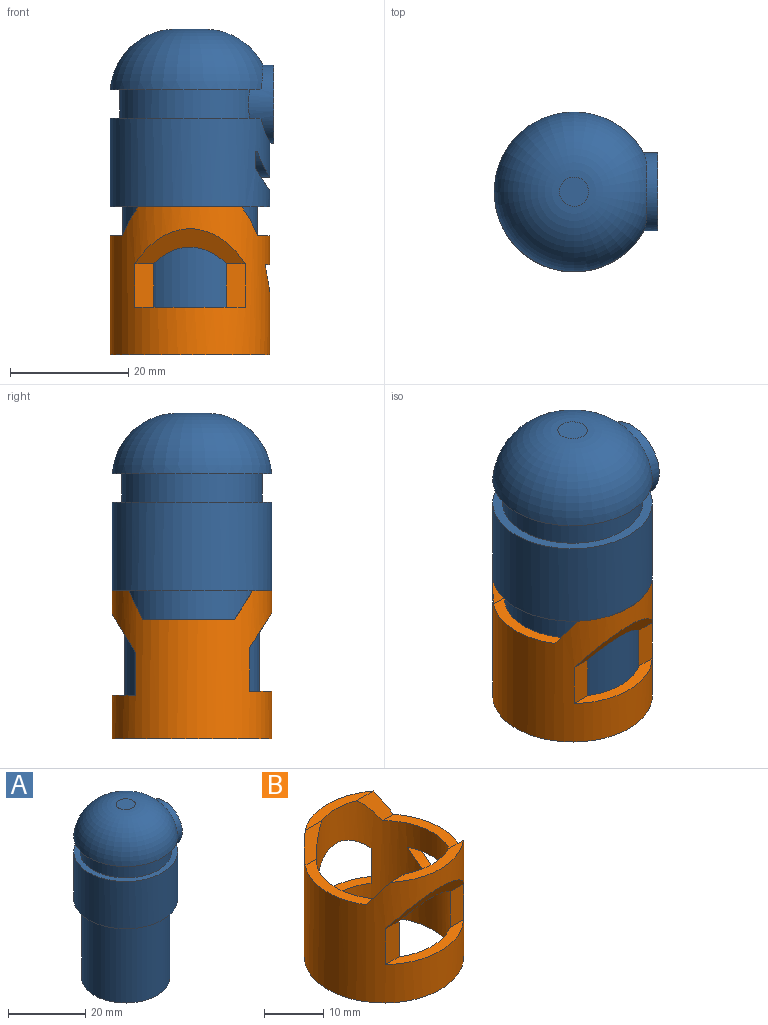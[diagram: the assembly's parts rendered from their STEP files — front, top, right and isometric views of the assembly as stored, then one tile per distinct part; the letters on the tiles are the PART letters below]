
ASSEMBLY  parts=2 mates=1
PART A: 18 faces, bbox 27.6x27x55 mm
  f0: torus R=2.48mm, axis (0,0,-1), area 927.2mm2, adj f1,f6,f7
  f1: plane 4.95x4.95mm, normal (0,0,1), area 19.3mm2, adj f0
  f2: plane 26.95x26.95mm, normal (0,0,-1), area 162.2mm2, adj f3,f16
  f3: cylinder r=13.48mm len=26.95mm, axis (0,0,-1), area 1189.7mm2, adj f2,f4,f7,f11,f12,f13,f14,f15
  f4: plane 26.95x25.47mm, normal (0,0,1), area 108.7mm2, adj f3,f5,f7
  f5: cylinder r=11.85mm len=23.69mm, axis (0,0,-1), area 289.4mm2, adj f4,f6,f7
  f6: plane 26.95x25.47mm, normal (0,0,-1), area 108.7mm2, adj f0,f5,f7
  f7: cylinder r=6.59mm len=13.18mm, axis (-1,0,0), area 91.5mm2, adj f0,f3,f4,f5,f6,f8
  f8: plane 13.18x13.18mm, normal (1,0,0), area 53.8mm2, adj f7,f9
  f9: cylinder r=5.13mm len=10.26mm, axis (1,0,0), area 93.4mm2, adj f8,f10
  f10: plane 10.26x10.26mm, normal (1,0,0), area 82.6mm2, adj f9
  f11: plane 0.53x0.35mm, normal (0,0,-1), area 0.1mm2, adj f3,f14,f15
  f12: cylinder r=9.85mm len=15.44mm, axis (1,0,0), area 27.6mm2, adj f3,f15
  f13: plane 0.53x0.35mm, normal (0,0,-1), area 0.1mm2, adj f3,f14,f15
  f14: cylinder r=8.06mm len=14.38mm, axis (1,0,0), area 28.9mm2, adj f3,f11,f13,f15
  f15: plane 15.44x6.59mm, normal (1,0,0), area 38.8mm2, adj f3,f11,f12,f13,f14
  f16: cylinder r=11.4mm len=25mm, axis (0,0,1), area 1790.7mm2, adj f2,f17
  f17: plane 22.8x22.8mm, normal (0,0,-1), area 408.3mm2, adj f16
PART B: 23 faces, bbox 27x27x25 mm
  f0: cylinder r=13.48mm len=26.96mm, axis (0,0,1), area 1415.5mm2, adj f2,f3,f4,f5,f6,f7,f8,f9
  f1: cylinder r=11.5mm len=25mm, axis (0,0,1), area 1322mm2, adj f2,f3,f4,f5,f6,f7,f8,f9
  f2: plane 7.42x3.21mm, normal (0,-1,0), area 23.8mm2, adj f0,f1,f10,f11
  f3: plane 7.29x3.1mm, normal (0,1,0), area 22.6mm2, adj f0,f1,f13,f15
  f4: plane 6.47x4.85mm, normal (0,-0.9,0.44), area 17.2mm2, adj f0,f1,f6,f7
  f5: plane 6.22x4.85mm, normal (0,0.84,0.54), area 16.4mm2, adj f0,f1,f6,f9
  f6: plane 15.5x5.55mm, normal (0,0,1), area 33.2mm2, adj f0,f1,f4,f5
  f7: plane 16.32x2.75mm, normal (0,0,1), area 26.3mm2, adj f0,f1,f4,f16
  f8: plane 26.96x26.96mm, normal (0,0,-1), area 155.6mm2, adj f0,f1
  f9: plane 17.5x3.22mm, normal (0,0,1), area 29.9mm2, adj f0,f1,f5,f17
  f10: plane 18.64x5.88mm, normal (0,-0.84,-0.54), area 62.2mm2, adj f0,f1,f2,f12
  f11: plane 18.64x3.74mm, normal (0,0,1), area 33.4mm2, adj f0,f1,f2,f12
  f12: plane 7.42x3.21mm, normal (0,-1,0), area 23.8mm2, adj f0,f1,f10,f11
  f13: plane 19.07x6.48mm, normal (0,0.85,-0.52), area 66.8mm2, adj f0,f1,f3,f14,f19
  f14: plane 7.29x3.1mm, normal (0,1,0), area 22.6mm2, adj f0,f1,f13,f15
  f15: plane 19.07x3.92mm, normal (0,0,1), area 34.7mm2, adj f0,f1,f3,f14,f20
  f16: plane 6.47x4.85mm, normal (0,-0.9,0.44), area 17.2mm2, adj f0,f1,f7,f18
  f17: plane 6.22x4.85mm, normal (0,0.84,0.54), area 16.4mm2, adj f0,f1,f9,f18
  f18: plane 15.5x5.55mm, normal (0,0,1), area 33.2mm2, adj f0,f1,f16,f17
  f19: plane 1x0.01mm, normal (0,0,-1), area 0mm2, adj f0,f13
  f20: plane 1.68x0.03mm, normal (0,0,1), area 0mm2, adj f0,f15
  f21: plane 9.42x3.05mm, normal (0,0,-1), area 19.1mm2, adj f0,f1,f22
  f22: extruded ~9.42x4.89mm, area 28.6mm2, adj f0,f1,f21
PLACE A t=(-17.62,7.52,5.87)mm
PLACE B t=(-64.53,7.52,5.87)mm
MATE revolute B.f0 <-> A.f0  axis (0,0,1) through (-20.1,7.52,5.87)mm
